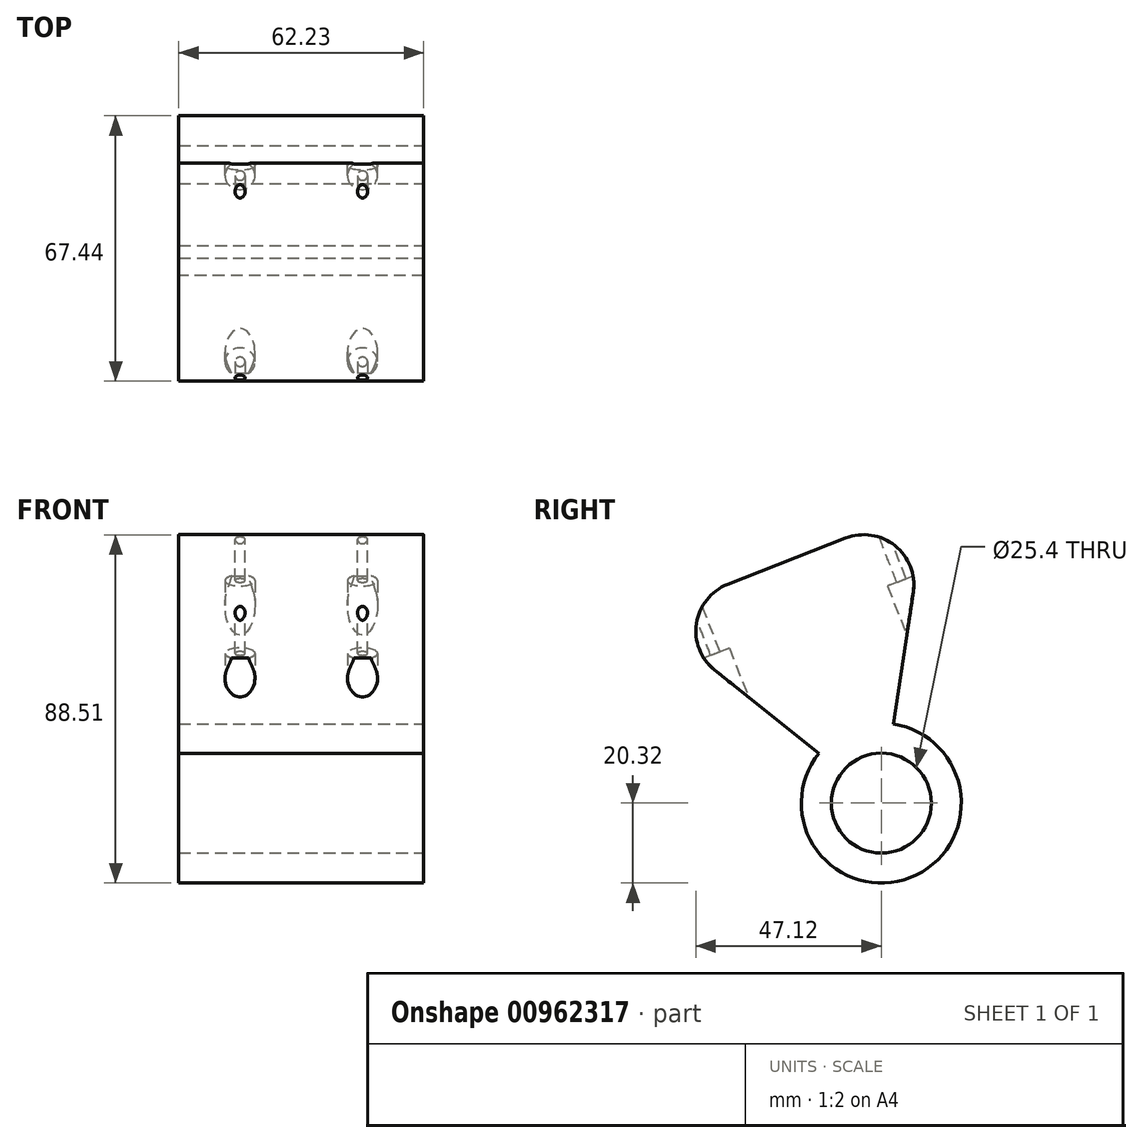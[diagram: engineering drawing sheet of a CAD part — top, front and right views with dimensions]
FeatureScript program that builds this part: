
annotation { "Feature Type Name" : "Feature", "Feature Type Description" : "" }
export const myFeature = defineFeature(function(context is Context, id is Id, definition is map)
    precondition{}
    {
        {
            var Q0;
            Q0=qCreatedBy(makeId("Right.planeOp"),FACE);
            var sketch = newSketch(context, id + "F0", { "sketchPlane" : qUnion([Q0])});
            skCircle(sketch, "E0", {"center": v(0, 0) * mm, "radius": 20.32 * mm});
            skSolve(sketch);
        }
        {
            var Q0;
            Q0=makeQuery(id+"F0.imprint","IMPRINT",FACE,{"disambiguationData":[TD([[makeQuery(id+"F0.imprint","IMPRINT",EDGE,{"derivedFrom":sQuery(id+"F0.wireOp",EDGE,"E0")}),1.0]])]});
            extrude(context, id + "F1", {"entities" : qUnion([Q0]), "depth" : 62.23 * mm, "offsetDistance" : 25.4 * mm});
        }
        {
            var Q0;
            Q0=makeQuery(id+"F1.opExtrude","CAP_FACE",FACE,{"disambiguationData":[OSD([sQuery(id+"F0.wireOp",EDGE,"E0")])],"isStart":false});
            var sketch = newSketch(context, id + "F2", { "sketchPlane" : qUnion([Q0])});
            skCircle(sketch, "E1", {"center": v(0, 0) * mm, "radius": 12.7 * mm});
            skSolve(sketch);
        }
        {
            var Q0;
            Q0=makeQuery(id+"F2.imprint","IMPRINT",FACE,{"disambiguationData":[TD([[makeQuery(id+"F2.imprint","IMPRINT",EDGE,{"derivedFrom":sQuery(id+"F2.wireOp",EDGE,"E1")}),1.0]])]});
            extrude(context, id + "F3", {"entities" : qUnion([Q0]), "operationType" : NewBodyOperationType.REMOVE, "oppositeDirection" : true, "depth" : 76.2 * mm, "offsetDistance" : 25.4 * mm});
        }
        {
            var Q0;
            Q0=makeQuery(id+"F1.opExtrude","CAP_FACE",FACE,{"disambiguationData":[OSD([sQuery(id+"F0.wireOp",EDGE,"E0")])],"isStart":false});
            var sketch = newSketch(context, id + "F4", { "sketchPlane" : qUnion([Q0])});
            skLineSegment(sketch, "E2", {"start": v(0, 0) * mm, "end": v(-22.4, 17.9) * mm});
            skLineSegment(sketch, "E3", {"start": v(0, 0) * mm, "end": v(6.57, 43.38) * mm});
            skLineSegment(sketch, "E4", {"start": v(0, 0) * mm, "end": v(-59.54, 47.56) * mm});
            skLineSegment(sketch, "E5", {"start": v(0, 0) * mm, "end": v(11.42, 75.34) * mm});
            skLineSegment(sketch, "E6", {"start": v(11.42, 75.34) * mm, "end": v(-59.54, 47.56) * mm});
            skSolve(sketch);
        }
        {
            var Q0;
            {var subQ0=sQuery(id+"F4.wireOp",EDGE,"E6");Q0=makeQuery(id+"F4.imprint","IMPRINT",FACE,{"disambiguationData":[TD([[makeQuery(id+"F4.imprint","IMPRINT",EDGE,{"derivedFrom":subQ0}),1.0]])]});}
            extrude(context, id + "F5", {"entities" : qUnion([Q0]), "operationType" : NewBodyOperationType.ADD, "oppositeDirection" : true, "depth" : 62.23 * mm, "offsetDistance" : 25.4 * mm});
        }
        {
            var Q0;
            {var subQ0=sQuery(id+"F0.wireOp",EDGE,"E0");var subQ1=sQuery(id+"F4.wireOp",EDGE,"E5");Q0=makeQuery(id+"F5.boolean.opBoolean","SPLIT",EDGE,{"disambiguationData":[topologyDisambiguationEdgeConnected([makeQuery(id+"F1.opExtrude","SWEPT_FACE",FACE,{"disambiguationData":[OSD([subQ0])]})])],"derivedFrom":makeQuery(id+"F5.opExtrude","SWEPT_EDGE",EDGE,{"disambiguationData":[OSD([subQ0,subQ1])]})});}
            var Q1;
            {var subQ0=sQuery(id+"F0.wireOp",EDGE,"E0");var subQ1=sQuery(id+"F4.wireOp",EDGE,"E4");Q1=makeQuery(id+"F5.boolean.opBoolean","SPLIT",EDGE,{"disambiguationData":[topologyDisambiguationEdgeConnected([makeQuery(id+"F1.opExtrude","SWEPT_FACE",FACE,{"disambiguationData":[OSD([subQ0])]})])],"derivedFrom":makeQuery(id+"F5.opExtrude","SWEPT_EDGE",EDGE,{"disambiguationData":[OSD([subQ0,subQ1])]})});}
            fillet(context, id + "F6", {"entities" : qUnion([Q0, Q1]), "radius" : 12.7 * mm, "tangentPropagation" : true, "allowEdgeOverflow" : false});
        }
        {
            var Q0;
            Q0=makeQuery(id+"F5.opExtrude","SWEPT_FACE",FACE,{"disambiguationData":[OSD([sQuery(id+"F4.wireOp",EDGE,"E6")])]});
            var sketch = newSketch(context, id + "F7", { "sketchPlane" : qUnion([Q0])});
            skLineSegment(sketch, "E7.0.0", {"start": v(62.23, -38.1) * mm, "end": v(62.23, 38.1) * mm});
            skLineSegment(sketch, "E7.0.1", {"start": v(62.23, 38.1) * mm, "end": v(0, 38.1) * mm});
            skLineSegment(sketch, "E7.0.2", {"start": v(0, 38.1) * mm, "end": v(0, -38.1) * mm});
            skLineSegment(sketch, "E7.0.3", {"start": v(0, -38.1) * mm, "end": v(62.23, -38.1) * mm});
            skLineSegment(sketch, "E8", {"start": v(31.12, -38.1) * mm, "end": v(31.12, -25.4) * mm, "construction": true});
            skLineSegment(sketch, "E9", {"start": v(0, -25.4) * mm, "end": v(31.12, -25.4) * mm, "construction": true});
            skLineSegment(sketch, "E10", {"start": v(31.12, -25.4) * mm, "end": v(62.23, -25.4) * mm, "construction": true});
            skPoint(sketch, "E11", {"position": v(15.56, -25.4) * mm});
            skPoint(sketch, "E12", {"position": v(46.67, -25.4) * mm});
            skLineSegment(sketch, "E13", {"start": v(0, 0) * mm, "end": v(62.23, 0) * mm, "construction": true});
            skPoint(sketch, "E14.MirrorP", {"position": v(15.56, 25.4) * mm});
            skPoint(sketch, "E15.MirrorP", {"position": v(46.67, 25.4) * mm});
            skSolve(sketch);
        }
        {
            var Q0;
            Q0=sQuery(id+"F7.wireOp",VERTEX,"E11");
            var Q1;
            Q1=sQuery(id+"F7.wireOp",VERTEX,"E14.MirrorP");
            var Q2;
            Q2=sQuery(id+"F7.wireOp",VERTEX,"E15.MirrorP");
            var Q3;
            Q3=sQuery(id+"F7.wireOp",VERTEX,"E12");
            var Q4;
            Q4=makeQuery(id+"F1.opExtrude","SWEPT_BODY",BODY,{"disambiguationData":[OSD([sQuery(id+"F0.wireOp",EDGE,"E0")])]});
            hole(context, id + "F8", {"style" : HoleStyle.SIMPLE, "endStyle" : HoleEndStyle.THROUGH, "holeDiameter" : 2.54 * mm, "majorDiameter" : 6.35 * mm, "isTappedThrough" : true, "tappedDepth" : 12.7 * mm, "tapClearance" : 3, "locations" : qUnion([Q0, Q1, Q2, Q3]), "scope" : qUnion([Q4])});
        }
        {
            var Q0;
            {var subQ0=sQuery(id+"F0.wireOp",EDGE,"E0");Q0=makeQuery(id+"F5.boolean.opBoolean","MERGE",FACE,{"derivedFrom":[makeQuery(id+"F1.opExtrude","CAP_FACE",FACE,{"disambiguationData":[OSD([subQ0])],"isStart":true}),makeQuery(id+"F5.opExtrude","CAP_FACE",FACE,{"disambiguationData":[OSD([subQ0,sQuery(id+"F4.wireOp",EDGE,"E4"),sQuery(id+"F4.wireOp",EDGE,"E5"),sQuery(id+"F4.wireOp",EDGE,"E6")])],"isStart":false})]});}
            var sketch = newSketch(context, id + "F9", { "sketchPlane" : qUnion([Q0])});
            skLineSegment(sketch, "E16", {"start": v(24.06, 61.45) * mm, "end": v(-7.4, -18.92) * mm});
            skLineSegment(sketch, "E17", {"start": v(-7.4, -18.92) * mm, "end": v(-50.53, -2.04) * mm});
            skSolve(sketch);
        }
        {
            var Q0;
            Q0=makeQuery(id+"F1.opExtrude","CAP_EDGE",EDGE,{"disambiguationData":[OSD([sQuery(id+"F0.wireOp",EDGE,"E0")])],"isStart":false});
            cPoint(context, id + "F10", {"entities" : qUnion([Q0]), "parameter" : 0.5});
        }
        {
            var Q0;
            Q0 = qCreatedBy(id + "F10" ,VERTEX);
            var Q1;
            Q1=sQuery(id+"F9.wireOp",VERTEX,"E16.end");
            var Q2;
            Q2=sQuery(id+"F9.wireOp",VERTEX,"E17.end");
            cPlane(context, id + "F11", {"entities" : qUnion([Q0, Q1, Q2]), "cplaneType" : CPlaneType.THREE_POINT, "offset" : 25.4 * mm, "width" : 152.4 * mm, "height" : 152.4 * mm});
        }
        {
            var Q0;
            Q0=qCreatedBy(id+"F11.planeOp",FACE);
            var sketch = newSketch(context, id + "F12", { "sketchPlane" : qUnion([Q0])});
            skCircle(sketch, "E18.0", {"center": v(46.67, -25.4) * mm, "radius": 1.27 * mm});
            skCircle(sketch, "E19.0", {"center": v(46.67, 25.4) * mm, "radius": 1.27 * mm});
            skCircle(sketch, "E20.0", {"center": v(15.56, 25.4) * mm, "radius": 1.27 * mm});
            skCircle(sketch, "E21.0", {"center": v(15.56, -25.4) * mm, "radius": 1.27 * mm});
            skCircle(sketch, "E22", {"center": v(46.67, -25.4) * mm, "radius": 3.81 * mm});
            skCircle(sketch, "E23", {"center": v(46.67, 25.4) * mm, "radius": 3.81 * mm});
            skCircle(sketch, "E24", {"center": v(15.56, 25.4) * mm, "radius": 3.81 * mm});
            skCircle(sketch, "E25", {"center": v(15.56, -25.4) * mm, "radius": 3.81 * mm});
            skSolve(sketch);
        }
        {
            var Q0;
            Q0=makeQuery(id+"F12.imprint","IMPRINT",FACE,{"disambiguationData":[TD([[makeQuery(id+"F12.imprint","IMPRINT",EDGE,{"derivedFrom":sQuery(id+"F12.wireOp",EDGE,"E18.0")}),-1.0]])]});
            var Q1;
            Q1=makeQuery(id+"F12.imprint","IMPRINT",FACE,{"disambiguationData":[TD([[makeQuery(id+"F12.imprint","IMPRINT",EDGE,{"derivedFrom":sQuery(id+"F12.wireOp",EDGE,"E19.0")}),-1.0]])]});
            var Q2;
            Q2=makeQuery(id+"F12.imprint","IMPRINT",FACE,{"disambiguationData":[TD([[makeQuery(id+"F12.imprint","IMPRINT",EDGE,{"derivedFrom":sQuery(id+"F12.wireOp",EDGE,"E20.0")}),-1.0]])]});
            var Q3;
            Q3=makeQuery(id+"F12.imprint","IMPRINT",FACE,{"disambiguationData":[TD([[makeQuery(id+"F12.imprint","IMPRINT",EDGE,{"derivedFrom":sQuery(id+"F12.wireOp",EDGE,"E21.0")}),-1.0]])]});
            extrude(context, id + "F13", {"entities" : qUnion([Q0, Q1, Q2, Q3]), "operationType" : NewBodyOperationType.REMOVE, "depth" : 71.12 * mm, "offsetDistance" : 25.4 * mm});
        }
    });
